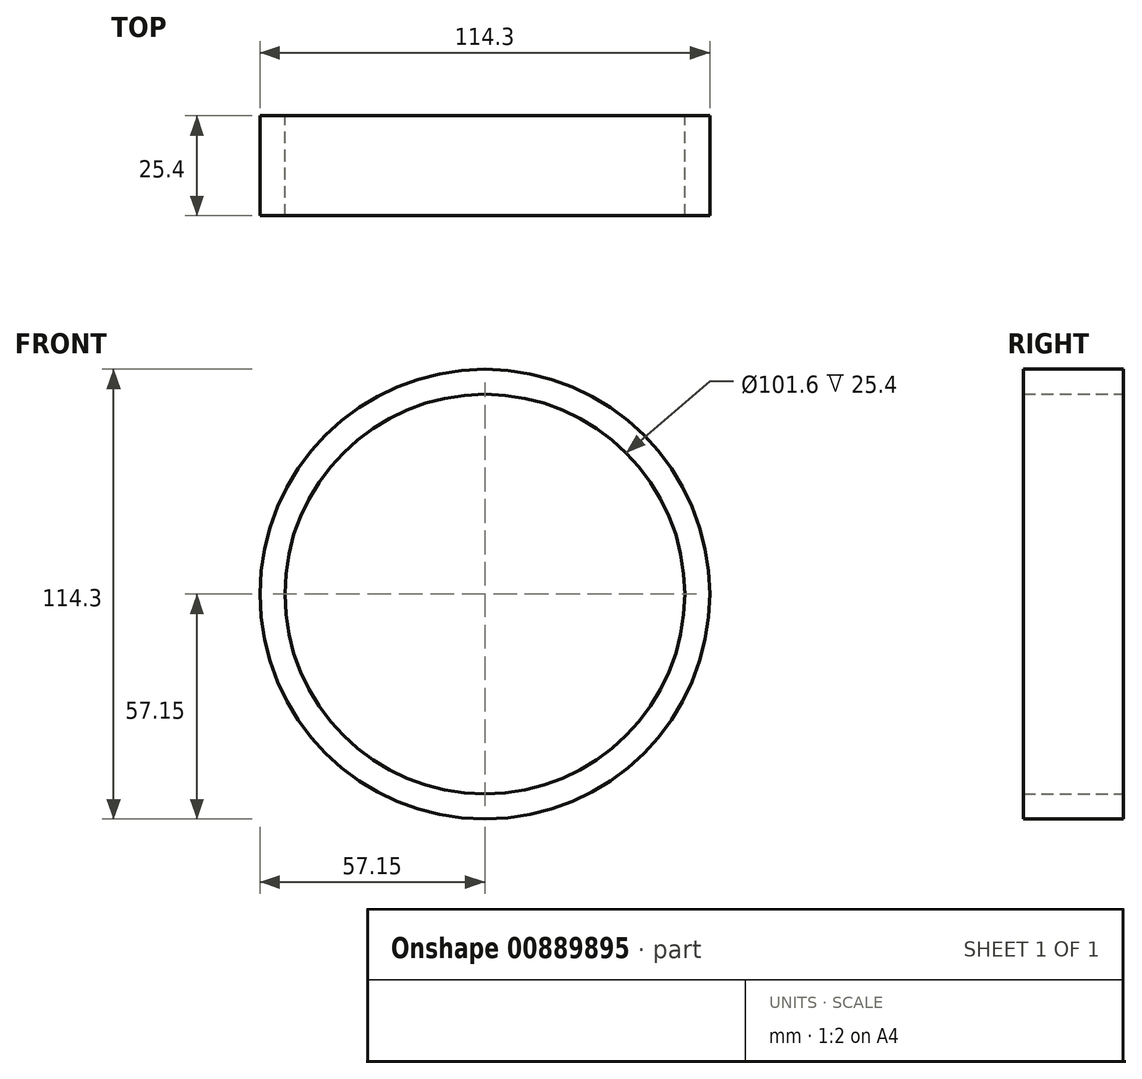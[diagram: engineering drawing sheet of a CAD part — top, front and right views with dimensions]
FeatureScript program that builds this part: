
annotation { "Feature Type Name" : "Feature", "Feature Type Description" : "" }
export const myFeature = defineFeature(function(context is Context, id is Id, definition is map)
    precondition{}
    {
        {
            var Q0;
            Q0=qCreatedBy(makeId("Front.planeOp"),FACE);
            var sketch = newSketch(context, id + "F0", { "sketchPlane" : qUnion([Q0])});
            skCircle(sketch, "E0", {"center": v(0, 0) * mm, "radius": 50.8 * mm});
            skCircle(sketch, "E1.0", {"center": v(0, 0) * mm, "radius": 57.15 * mm});
            skSolve(sketch);
        }
        {
            var Q0;
            Q0=makeQuery(id+"F0.imprint","IMPRINT",FACE,{"disambiguationData":[TD([[makeQuery(id+"F0.imprint","IMPRINT",EDGE,{"derivedFrom":sQuery(id+"F0.wireOp",EDGE,"E0")}),-1.0]])]});
            var Q1;
            Q1=sQuery(id+"F0.wireOp",EDGE,"E1.0");
            extrude(context, id + "F1", {"entities" : qUnion([Q0]), "surfaceEntities" : qUnion([Q1]), "endBound" : BoundingType.SYMMETRIC, "depth" : 25.4 * mm, "offsetDistance" : 25.4 * mm});
        }
    });
